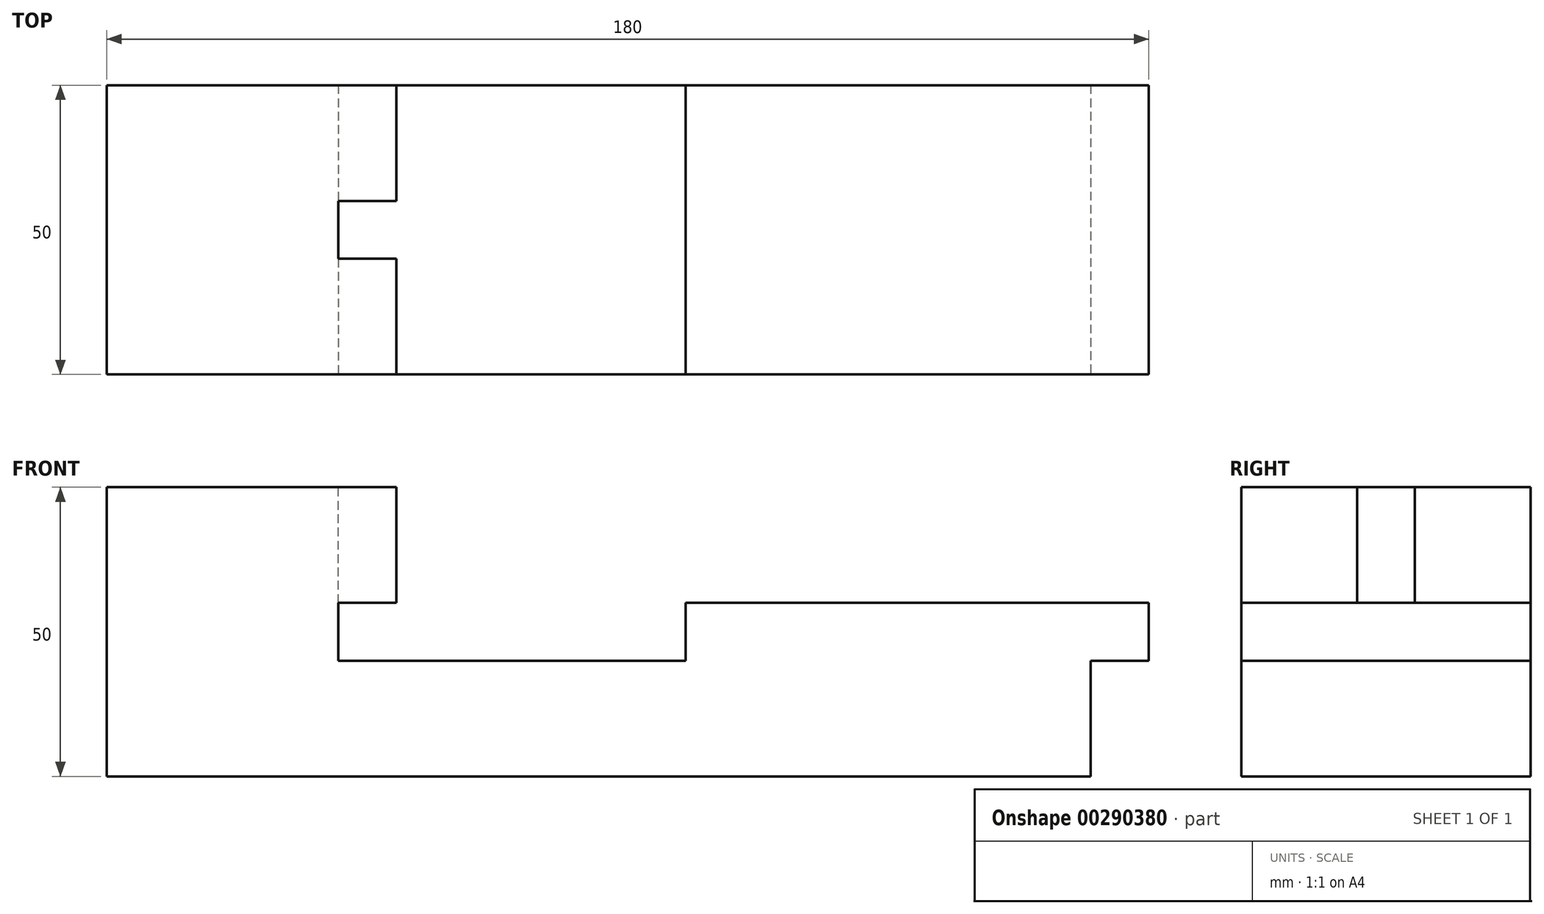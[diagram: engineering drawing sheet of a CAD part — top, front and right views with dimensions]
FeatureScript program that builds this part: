
annotation { "Feature Type Name" : "Feature", "Feature Type Description" : "" }
export const myFeature = defineFeature(function(context is Context, id is Id, definition is map)
    precondition{}
    {
        {
            var Q0;
            Q0=qCreatedBy(makeId("Right.planeOp"),FACE);
            var sketch = newSketch(context, id + "F0", { "sketchPlane" : qUnion([Q0])});
            skLineSegment(sketch, "E0.bottom", {"start": v(25, 25) * mm, "end": v(-25, 25) * mm});
            skLineSegment(sketch, "E0.top", {"start": v(25, -25) * mm, "end": v(-25, -25) * mm});
            skLineSegment(sketch, "E0.left", {"start": v(25, 25) * mm, "end": v(25, -25) * mm});
            skLineSegment(sketch, "E0.right", {"start": v(-25, 25) * mm, "end": v(-25, -25) * mm});
            skPoint(sketch, "E0.middle", {"position": v(0, 0) * mm});
            skSolve(sketch);
        }
        {
            var Q0;
            Q0 = qSketchRegion(id + "F0", true);
            extrude(context, id + "F1", {"entities" : qUnion([Q0]), "endBound" : BoundingType.SYMMETRIC, "depth" : 200 * mm});
        }
        {
            var Q0;
            Q0=makeQuery(id+"F1.opExtrude","SWEPT_FACE",FACE,{"disambiguationData":[OSD([sQuery(id+"F0.wireOp",EDGE,"E0.right")])]});
            var sketch = newSketch(context, id + "F2", { "sketchPlane" : qUnion([Q0])});
            skLineSegment(sketch, "E1", {"start": v(-60, -5) * mm, "end": v(0, -5) * mm});
            skLineSegment(sketch, "E2", {"start": v(0, -5) * mm, "end": v(0, 5) * mm});
            skLineSegment(sketch, "E3", {"start": v(0, 5) * mm, "end": v(80, 5) * mm});
            skLineSegment(sketch, "E4", {"start": v(80, 5) * mm, "end": v(80, -5) * mm});
            skLineSegment(sketch, "E5", {"start": v(80, -5) * mm, "end": v(70, -5) * mm});
            skLineSegment(sketch, "E6", {"start": v(70, -5) * mm, "end": v(70, -25) * mm});
            skLineSegment(sketch, "E7", {"start": v(-60, -5) * mm, "end": v(-60, 5) * mm});
            skLineSegment(sketch, "E8", {"start": v(-60, 5) * mm, "end": v(-50, 5) * mm});
            skLineSegment(sketch, "E9", {"start": v(-50, 5) * mm, "end": v(-50, 25) * mm});
            skLineSegment(sketch, "E10", {"start": v(-50, 25) * mm, "end": v(100, 25) * mm});
            skLineSegment(sketch, "E11", {"start": v(100, 25) * mm, "end": v(100, -25) * mm});
            skLineSegment(sketch, "E12", {"start": v(100, -25) * mm, "end": v(70, -25) * mm});
            skSolve(sketch);
        }
        {
            var Q0;
            Q0 = qSketchRegion(id + "F2", true);
            extrude(context, id + "F3", {"entities" : qUnion([Q0]), "operationType" : NewBodyOperationType.REMOVE, "endBound" : BoundingType.UP_TO_NEXT, "oppositeDirection" : true, "depth" : 25 * mm});
        }
        {
            var Q0;
            Q0=makeQuery(id+"F1.opExtrude","SWEPT_FACE",FACE,{"disambiguationData":[OSD([sQuery(id+"F0.wireOp",EDGE,"E0.bottom")])]});
            var sketch = newSketch(context, id + "F4", { "sketchPlane" : qUnion([Q0])});
            skLineSegment(sketch, "E13", {"start": v(-50, 0) * mm, "end": v(-100, 0) * mm, "construction": true});
            skLineSegment(sketch, "E14.bottom", {"start": v(-50, 5) * mm, "end": v(-60, 5) * mm});
            skLineSegment(sketch, "E14.top", {"start": v(-50, -5) * mm, "end": v(-60, -5) * mm});
            skLineSegment(sketch, "E14.left", {"start": v(-50, 5) * mm, "end": v(-50, -5) * mm});
            skLineSegment(sketch, "E14.right", {"start": v(-60, 5) * mm, "end": v(-60, -5) * mm});
            skSolve(sketch);
        }
        {
            var Q0;
            Q0 = qSketchRegion(id + "F4", true);
            extrude(context, id + "F5", {"entities" : qUnion([Q0]), "operationType" : NewBodyOperationType.REMOVE, "endBound" : BoundingType.UP_TO_NEXT, "oppositeDirection" : true, "depth" : 25 * mm});
        }
    });
